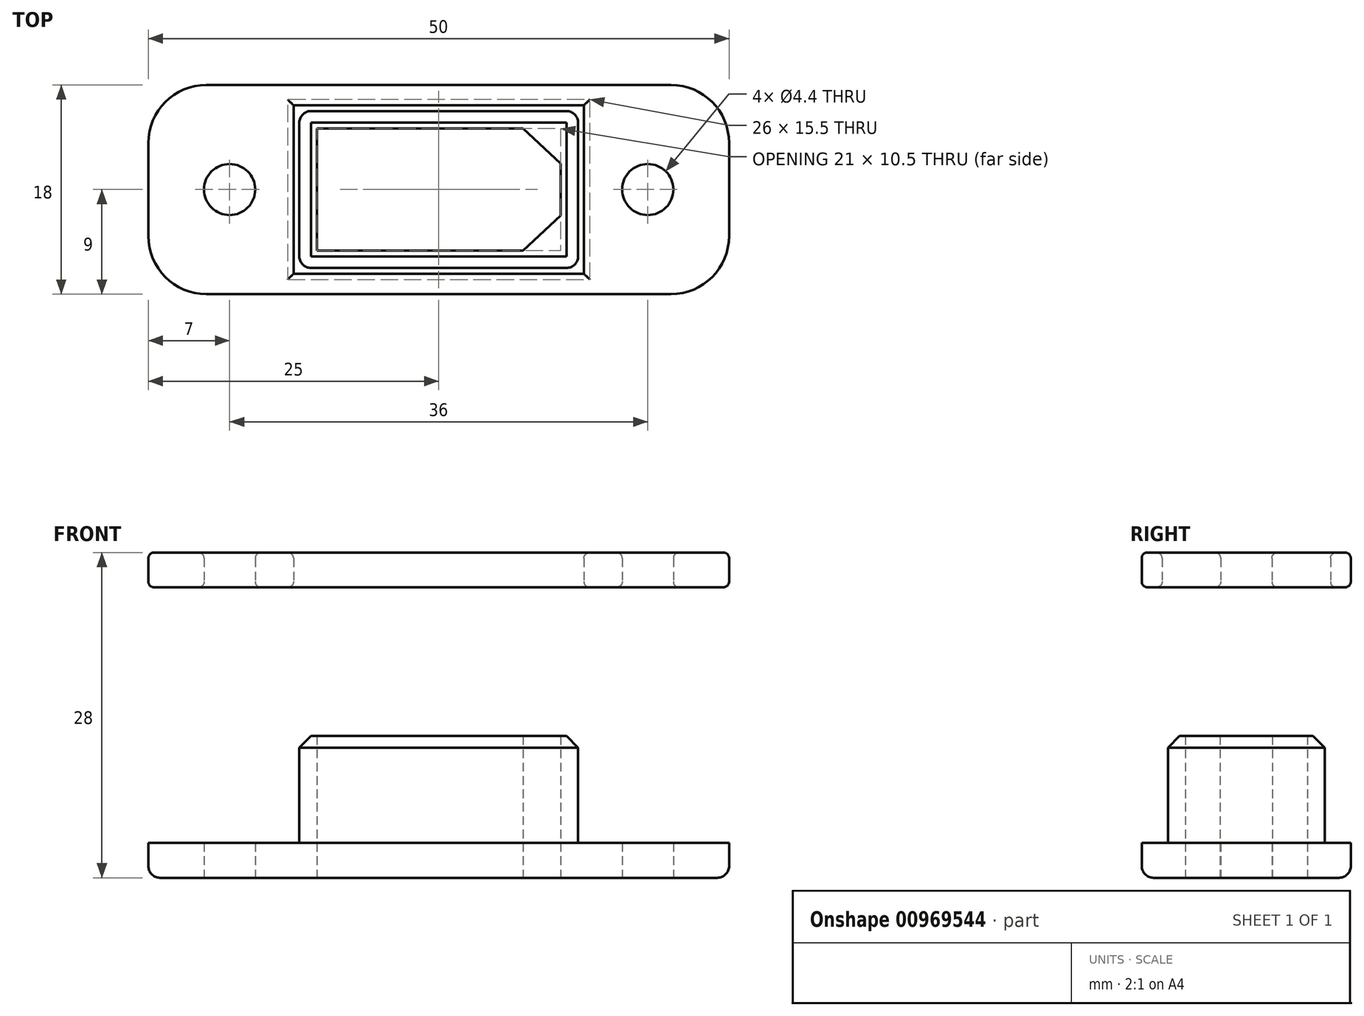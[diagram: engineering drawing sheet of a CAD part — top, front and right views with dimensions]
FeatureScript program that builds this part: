
annotation { "Feature Type Name" : "Feature", "Feature Type Description" : "" }
export const myFeature = defineFeature(function(context is Context, id is Id, definition is map)
    precondition{}
    {
        {
            var Q0;
            Q0=qCreatedBy(makeId("Top.planeOp"),FACE);
            var sketch = newSketch(context, id + "F0", { "sketchPlane" : qUnion([Q0])});
            skLineSegment(sketch, "E0.bottom", {"start": v(-25, 9) * mm, "end": v(25, 9) * mm});
            skLineSegment(sketch, "E0.top", {"start": v(-25, -9) * mm, "end": v(25, -9) * mm});
            skLineSegment(sketch, "E0.left", {"start": v(-25, 9) * mm, "end": v(-25, -9) * mm});
            skLineSegment(sketch, "E0.right", {"start": v(25, 9) * mm, "end": v(25, -9) * mm});
            skPoint(sketch, "E0.middle", {"position": v(0, 0) * mm});
            skLineSegment(sketch, "E1.bottom", {"start": v(10.5, 5.25) * mm, "end": v(-10.5, 5.25) * mm});
            skLineSegment(sketch, "E1.top", {"start": v(10.5, -5.25) * mm, "end": v(-10.5, -5.25) * mm});
            skLineSegment(sketch, "E1.left", {"start": v(10.5, 5.25) * mm, "end": v(10.5, -5.25) * mm});
            skLineSegment(sketch, "E1.right", {"start": v(-10.5, 5.25) * mm, "end": v(-10.5, -5.25) * mm});
            skCircle(sketch, "E2", {"center": v(-18, 0) * mm, "radius": 2.2 * mm});
            skCircle(sketch, "E3", {"center": v(18, 0) * mm, "radius": 2.2 * mm});
            skLineSegment(sketch, "E4", {"start": v(-25, 0) * mm, "end": v(-18, 0) * mm, "construction": true});
            skLineSegment(sketch, "E5", {"start": v(-18, 0) * mm, "end": v(-10.5, 0) * mm, "construction": true});
            skLineSegment(sketch, "E6", {"start": v(18, 0) * mm, "end": v(25, 0) * mm, "construction": true});
            skSolve(sketch);
        }
        {
            var Q0;
            Q0=qSketchRegion(id+"F0",true);
            extrude(context, id + "F1", {"entities" : qUnion([Q0]), "depth" : 3 * mm, "offsetDistance" : 25 * mm});
        }
        {
            var Q0;
            Q0=makeQuery(id+"F1.opExtrude","CAP_FACE",FACE,{"disambiguationData":[OSD([sQuery(id+"F0.wireOp",EDGE,"E0.bottom"),sQuery(id+"F0.wireOp",EDGE,"E0.top"),sQuery(id+"F0.wireOp",EDGE,"E0.left"),sQuery(id+"F0.wireOp",EDGE,"E0.right"),sQuery(id+"F0.wireOp",EDGE,"E1.bottom"),sQuery(id+"F0.wireOp",EDGE,"E1.top"),sQuery(id+"F0.wireOp",EDGE,"E1.left"),sQuery(id+"F0.wireOp",EDGE,"E1.right"),sQuery(id+"F0.wireOp",EDGE,"E2"),sQuery(id+"F0.wireOp",EDGE,"E3")])],"isStart":false});
            var sketch = newSketch(context, id + "F2", { "sketchPlane" : qUnion([Q0])});
            skLineSegment(sketch, "E7.bottom", {"start": v(7.25, 5.25) * mm, "end": v(-10.5, 5.25) * mm});
            skLineSegment(sketch, "E7.top", {"start": v(7.25, -5.25) * mm, "end": v(-10.5, -5.25) * mm});
            skLineSegment(sketch, "E7.left", {"start": v(10.5, 2.25) * mm, "end": v(10.5, -2.25) * mm});
            skLineSegment(sketch, "E7.right", {"start": v(-10.5, 5.25) * mm, "end": v(-10.5, -5.25) * mm});
            skPoint(sketch, "E7.middle", {"position": v(0, 0) * mm});
            skLineSegment(sketch, "E8.bottom", {"start": v(12, 6.75) * mm, "end": v(-12, 6.75) * mm});
            skLineSegment(sketch, "E8.top", {"start": v(12, -6.75) * mm, "end": v(-12, -6.75) * mm});
            skLineSegment(sketch, "E8.left", {"start": v(12, 6.75) * mm, "end": v(12, -6.75) * mm});
            skLineSegment(sketch, "E8.right", {"start": v(-12, 6.75) * mm, "end": v(-12, -6.75) * mm});
            skLineSegment(sketch, "E9", {"start": v(0, 0) * mm, "end": v(10, 0) * mm, "construction": true});
            skLineSegment(sketch, "E10", {"start": v(10.5, -2.25) * mm, "end": v(7.25, -5.25) * mm});
            skLineSegment(sketch, "E11.MirrorCS", {"start": v(10.5, 2.25) * mm, "end": v(7.25, 5.25) * mm});
            skPoint(sketch, "E12.orphan", {"position": v(10.5, -5.25) * mm});
            skPoint(sketch, "E13.orphan", {"position": v(10.5, 5.25) * mm});
            skSolve(sketch);
        }
        {
            var Q0;
            Q0=qSketchRegion(id+"F2",true);
            extrude(context, id + "F3", {"entities" : qUnion([Q0]), "operationType" : NewBodyOperationType.ADD, "depth" : 9.2 * mm, "offsetDistance" : 25 * mm, "hasSecondDirection" : true, "secondDirectionOppositeDirection" : true, "secondDirectionDepth" : 3 * mm});
        }
        {
            var Q0;
            Q0=makeQuery(id+"F1.opExtrude","SWEPT_EDGE",EDGE,{"disambiguationData":[OSD([sQuery(id+"F0.wireOp",EDGE,"E0.top"),sQuery(id+"F0.wireOp",EDGE,"E0.left")])]});
            var Q1;
            Q1=makeQuery(id+"F1.opExtrude","SWEPT_EDGE",EDGE,{"disambiguationData":[OSD([sQuery(id+"F0.wireOp",EDGE,"E0.bottom"),sQuery(id+"F0.wireOp",EDGE,"E0.left")])]});
            var Q2;
            Q2=makeQuery(id+"F1.opExtrude","SWEPT_EDGE",EDGE,{"disambiguationData":[OSD([sQuery(id+"F0.wireOp",EDGE,"E0.bottom"),sQuery(id+"F0.wireOp",EDGE,"E0.right")])]});
            var Q3;
            Q3=makeQuery(id+"F1.opExtrude","SWEPT_EDGE",EDGE,{"disambiguationData":[OSD([sQuery(id+"F0.wireOp",EDGE,"E0.top"),sQuery(id+"F0.wireOp",EDGE,"E0.right")])]});
            fillet(context, id + "F4", {"entities" : qUnion([Q0, Q1, Q2, Q3]), "radius" : 5 * mm, "tangentPropagation" : true, "allowEdgeOverflow" : false});
        }
        {
            var Q0;
            Q0=makeQuery(id+"F1.opExtrude","CAP_EDGE",EDGE,{"disambiguationData":[OSD([sQuery(id+"F0.wireOp",EDGE,"E0.bottom")])],"isStart":true});
            fillet(context, id + "F5", {"entities" : qUnion([Q0]), "radius" : 1 * mm, "tangentPropagation" : true, "allowEdgeOverflow" : false});
        }
        {
            var Q0;
            Q0=makeQuery(id+"F0.imprint","IMPRINT",FACE,{"disambiguationData":[TD([[makeQuery(id+"F0.imprint","IMPRINT",EDGE,{"derivedFrom":sQuery(id+"F0.wireOp",EDGE,"E0.bottom")}),-1.0]])]});
            var sketch = newSketch(context, id + "F6", { "sketchPlane" : qUnion([Q0])});
            skCircle(sketch, "E14", {"center": v(18, 0) * mm, "radius": 4.75 * mm});
            skCircle(sketch, "E15", {"center": v(-18, 0) * mm, "radius": 4.75 * mm});
            skSolve(sketch);
        }
        {
            var Q0;
            Q0=makeQuery(id+"F3.opExtrude","SWEPT_EDGE",EDGE,{"disambiguationData":[OSD([sQuery(id+"F2.wireOp",EDGE,"E8.bottom"),sQuery(id+"F2.wireOp",EDGE,"E8.right")])]});
            var Q1;
            Q1=makeQuery(id+"F3.opExtrude","SWEPT_EDGE",EDGE,{"disambiguationData":[OSD([sQuery(id+"F2.wireOp",EDGE,"E8.bottom"),sQuery(id+"F2.wireOp",EDGE,"E8.left")])]});
            var Q2;
            Q2=makeQuery(id+"F3.opExtrude","SWEPT_EDGE",EDGE,{"disambiguationData":[OSD([sQuery(id+"F2.wireOp",EDGE,"E8.top"),sQuery(id+"F2.wireOp",EDGE,"E8.left")])]});
            var Q3;
            Q3=makeQuery(id+"F3.opExtrude","SWEPT_EDGE",EDGE,{"disambiguationData":[OSD([sQuery(id+"F2.wireOp",EDGE,"E8.top"),sQuery(id+"F2.wireOp",EDGE,"E8.right")])]});
            fillet(context, id + "F7", {"entities" : qUnion([Q0, Q1, Q2, Q3]), "radius" : 1 * mm, "tangentPropagation" : true, "allowEdgeOverflow" : false});
        }
        {
            var Q0;
            Q0=makeQuery(id+"F3.opExtrude","CAP_EDGE",EDGE,{"disambiguationData":[OSD([sQuery(id+"F2.wireOp",EDGE,"E8.bottom")])],"isStart":false});
            var Q1;
            {var subQ0=sQuery(id+"F2.wireOp",EDGE,"E8.right");var subQ1=sQuery(id+"F2.wireOp",EDGE,"E8.bottom");Q1=makeQuery(id+"F7.opFillet","BLEND_EDGE",EDGE,{"blendedFrom":[makeQuery(id+"F3.opExtrude","SWEPT_EDGE",EDGE,{"disambiguationData":[OSD([subQ1,subQ0])]}),makeQuery(id+"F3.opExtrude","CAP_FACE",FACE,{"disambiguationData":[OSD([sQuery(id+"F2.wireOp",EDGE,"E7.bottom"),sQuery(id+"F2.wireOp",EDGE,"E7.top"),sQuery(id+"F2.wireOp",EDGE,"E7.left"),sQuery(id+"F2.wireOp",EDGE,"E7.right"),subQ1,sQuery(id+"F2.wireOp",EDGE,"E8.top"),sQuery(id+"F2.wireOp",EDGE,"E8.left"),subQ0])],"isStart":false})],"blendedInto":[makeQuery(id+"F3.opExtrude","CAP_FACE",FACE,{"disambiguationData":[OSD([sQuery(id+"F2.wireOp",EDGE,"E7.bottom"),sQuery(id+"F2.wireOp",EDGE,"E7.top"),sQuery(id+"F2.wireOp",EDGE,"E7.left"),sQuery(id+"F2.wireOp",EDGE,"E7.right"),subQ1,sQuery(id+"F2.wireOp",EDGE,"E8.top"),sQuery(id+"F2.wireOp",EDGE,"E8.left"),subQ0])],"isStart":false})]});}
            var Q2;
            Q2=makeQuery(id+"F3.opExtrude","CAP_EDGE",EDGE,{"disambiguationData":[OSD([sQuery(id+"F2.wireOp",EDGE,"E8.right")])],"isStart":false});
            chamfer(context, id + "F8", {"entities" : qUnion([Q0, Q1, Q2]), "width" : 1 * mm, "tangentPropagation" : true});
        }
        {
            var Q0;
            Q0=makeQuery(id+"F1.opExtrude","CAP_FACE",FACE,{"disambiguationData":[OSD([sQuery(id+"F0.wireOp",EDGE,"E0.bottom"),sQuery(id+"F0.wireOp",EDGE,"E0.top"),sQuery(id+"F0.wireOp",EDGE,"E0.left"),sQuery(id+"F0.wireOp",EDGE,"E0.right"),sQuery(id+"F0.wireOp",EDGE,"E1.bottom"),sQuery(id+"F0.wireOp",EDGE,"E1.top"),sQuery(id+"F0.wireOp",EDGE,"E1.left"),sQuery(id+"F0.wireOp",EDGE,"E1.right"),sQuery(id+"F0.wireOp",EDGE,"E2"),sQuery(id+"F0.wireOp",EDGE,"E3")])],"isStart":false});
            var sketch = newSketch(context, id + "F9", { "sketchPlane" : qUnion([Q0])});
            skLineSegment(sketch, "E16.bottom", {"start": v(-12.5, 7.25) * mm, "end": v(12.5, 7.25) * mm});
            skLineSegment(sketch, "E16.top", {"start": v(-12.5, -7.25) * mm, "end": v(12.5, -7.25) * mm});
            skLineSegment(sketch, "E16.left", {"start": v(-12.5, 7.25) * mm, "end": v(-12.5, -7.25) * mm});
            skLineSegment(sketch, "E16.right", {"start": v(12.5, 7.25) * mm, "end": v(12.5, -7.25) * mm});
            skPoint(sketch, "E16.middle", {"position": v(0, 0) * mm});
            skPoint(sketch, "E16.middle.positionSnap0", {"position": v(0, 0) * mm});
            skPoint(sketch, "E16.centerSnap0", {"position": v(0, 0) * mm});
            skSolve(sketch);
        }
        {
            var Q0;
            {var subQ5=sQuery(id+"F0.wireOp",EDGE,"E2");Q0=makeQuery(id+"F9.imprint","IMPRINT",FACE,{"disambiguationData":[TD([[makeQuery(id+"F9.imprint","IMPRINT",EDGE,{"derivedFrom":makeQuery(id+"F1.opExtrude","CAP_EDGE",EDGE,{"disambiguationData":[OSD([subQ5])],"isStart":false})}),-1.0]])]});}
            extrude(context, id + "F10", {"entities" : qUnion([Q0]), "depth" : 25 * mm, "offsetDistance" : 25 * mm, "hasSecondDirection" : true, "secondDirectionOppositeDirection" : false, "secondDirectionDepth" : 22 * mm});
        }
        {
            var Q0;
            Q0=makeQuery(id+"F10.opExtrude","CAP_FACE",FACE,{"disambiguationData":[OSD([sQuery(id+"F0.wireOp",EDGE,"E0.bottom"),sQuery(id+"F0.wireOp",EDGE,"E0.top"),sQuery(id+"F0.wireOp",EDGE,"E0.left"),sQuery(id+"F0.wireOp",EDGE,"E0.right"),sQuery(id+"F0.wireOp",EDGE,"E1.bottom"),sQuery(id+"F0.wireOp",EDGE,"E1.top"),sQuery(id+"F0.wireOp",EDGE,"E1.left"),sQuery(id+"F0.wireOp",EDGE,"E1.right"),sQuery(id+"F0.wireOp",EDGE,"E2"),sQuery(id+"F0.wireOp",EDGE,"E3"),sQuery(id+"F2.wireOp",EDGE,"E8.bottom"),sQuery(id+"F2.wireOp",EDGE,"E8.top"),sQuery(id+"F2.wireOp",EDGE,"E8.left"),sQuery(id+"F2.wireOp",EDGE,"E8.right")])],"isStart":true});
            var Q1;
            Q1=makeQuery(id+"F10.opExtrude","CAP_FACE",FACE,{"disambiguationData":[OSD([sQuery(id+"F0.wireOp",EDGE,"E0.bottom"),sQuery(id+"F0.wireOp",EDGE,"E0.top"),sQuery(id+"F0.wireOp",EDGE,"E0.left"),sQuery(id+"F0.wireOp",EDGE,"E0.right"),sQuery(id+"F0.wireOp",EDGE,"E1.bottom"),sQuery(id+"F0.wireOp",EDGE,"E1.top"),sQuery(id+"F0.wireOp",EDGE,"E1.left"),sQuery(id+"F0.wireOp",EDGE,"E1.right"),sQuery(id+"F0.wireOp",EDGE,"E2"),sQuery(id+"F0.wireOp",EDGE,"E3"),sQuery(id+"F2.wireOp",EDGE,"E8.bottom"),sQuery(id+"F2.wireOp",EDGE,"E8.top"),sQuery(id+"F2.wireOp",EDGE,"E8.left"),sQuery(id+"F2.wireOp",EDGE,"E8.right")])],"isStart":false});
            fillet(context, id + "F11", {"entities" : qUnion([Q0, Q1]), "radius" : 0.5 * mm, "tangentPropagation" : true, "allowEdgeOverflow" : false});
        }
    });
